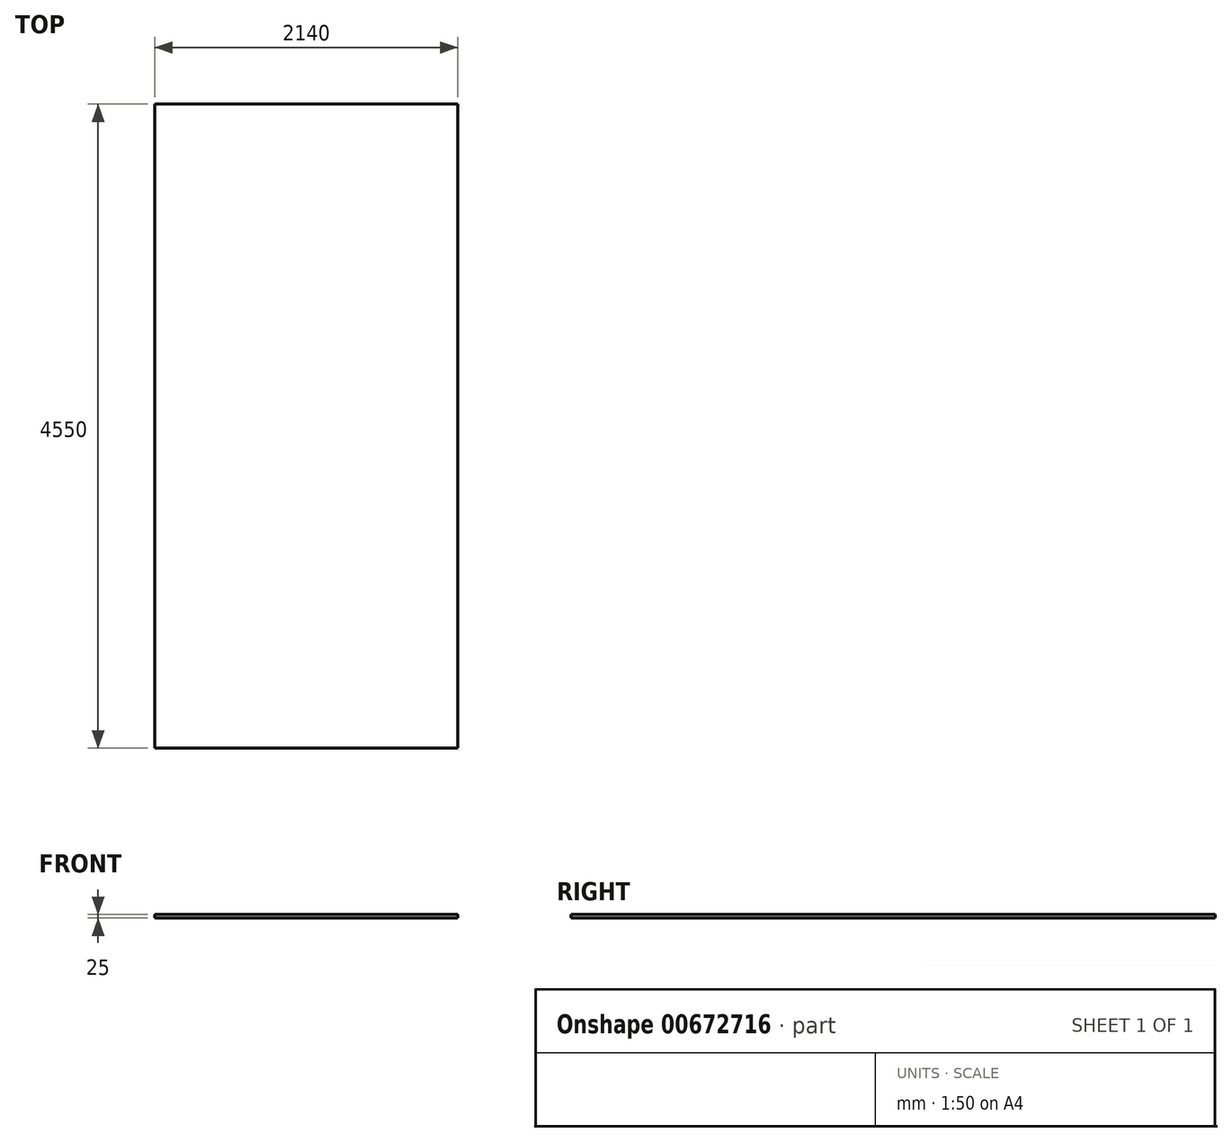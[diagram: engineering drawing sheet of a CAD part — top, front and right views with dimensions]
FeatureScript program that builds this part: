
annotation { "Feature Type Name" : "Feature", "Feature Type Description" : "" }
export const myFeature = defineFeature(function(context is Context, id is Id, definition is map)
    precondition{}
    {
        {
            var Q0;
            Q0=qCreatedBy(makeId("Top.planeOp"),FACE);
            var sketch = newSketch(context, id + "F0", { "sketchPlane" : qUnion([Q0])});
            skLineSegment(sketch, "E0.bottom", {"start": v(0, 0) * mm, "end": v(2140, 0) * mm});
            skLineSegment(sketch, "E0.top", {"start": v(0, 4550) * mm, "end": v(2140, 4550) * mm});
            skLineSegment(sketch, "E0.left", {"start": v(0, 0) * mm, "end": v(0, 4550) * mm});
            skLineSegment(sketch, "E0.right", {"start": v(2140, 0) * mm, "end": v(2140, 4550) * mm});
            skSolve(sketch);
        }
        {
            var Q0;
            Q0=makeQuery(id+"F0.imprint","IMPRINT",FACE,{"disambiguationData":[TD([[makeQuery(id+"F0.imprint","IMPRINT",EDGE,{"derivedFrom":sQuery(id+"F0.wireOp",EDGE,"E0.bottom")}),1.0]])]});
            extrude(context, id + "F1", {"entities" : qUnion([Q0]), "depth" : 25 * mm, "offsetDistance" : 25 * mm});
        }
    });
